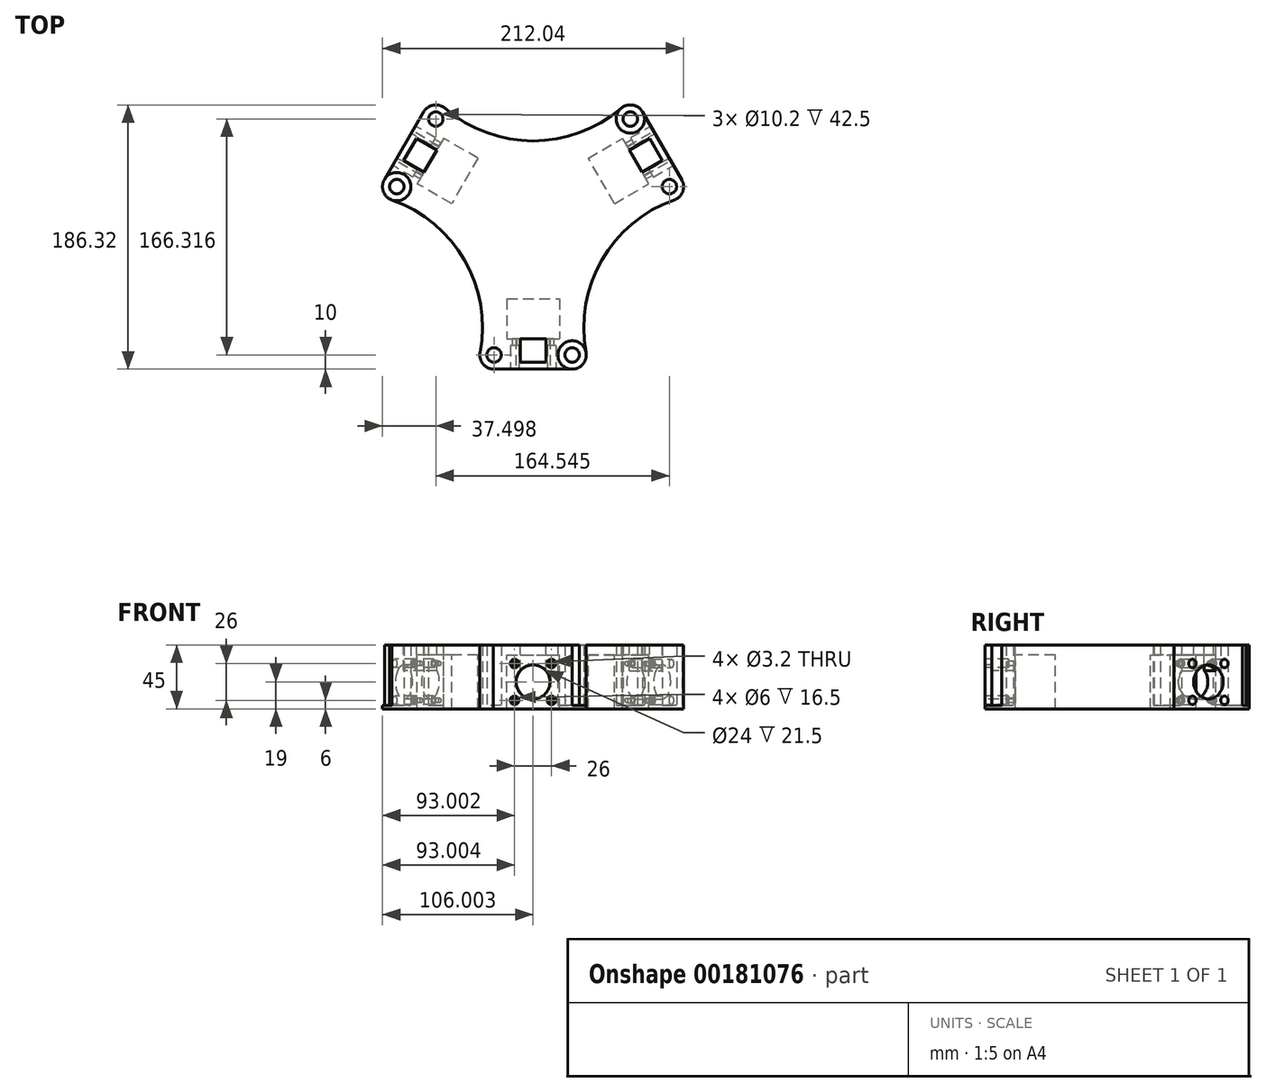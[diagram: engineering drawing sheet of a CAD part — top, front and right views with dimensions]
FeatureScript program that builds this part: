
annotation { "Feature Type Name" : "Feature", "Feature Type Description" : "" }
export const myFeature = defineFeature(function(context is Context, id is Id, definition is map)
    precondition{}
    {
        {
            var Q0;
            Q0=qCreatedBy(makeId("Top.planeOp"),FACE);
            var sketch = newSketch(context, id + "F0", { "sketchPlane" : qUnion([Q0])});
            skCircle(sketch, "E0", {"center": v(0, 0) * mm, "radius": 57.15 * mm, "construction": true});
            skLineSegment(sketch, "E1.bottom", {"start": v(110, -110) * mm, "end": v(-110, -110) * mm, "construction": true});
            skLineSegment(sketch, "E1.top", {"start": v(110, 110) * mm, "end": v(-110, 110) * mm, "construction": true});
            skLineSegment(sketch, "E1.left", {"start": v(110, -110) * mm, "end": v(110, 110) * mm, "construction": true});
            skLineSegment(sketch, "E1.right", {"start": v(-110, -110) * mm, "end": v(-110, 110) * mm, "construction": true});
            skLineSegment(sketch, "E2", {"start": v(0, 0) * mm, "end": v(-80.99, -46.76) * mm});
            skLineSegment(sketch, "E3", {"start": v(0, 0) * mm, "end": v(-84.59, 48.84) * mm});
            skLineSegment(sketch, "E4", {"start": v(0, 0) * mm, "end": v(0, -95) * mm});
            skLineSegment(sketch, "E5.MirrorCS", {"start": v(0, 0) * mm, "end": v(80.99, -46.76) * mm});
            skLineSegment(sketch, "E6.MirrorCS", {"start": v(0, 0) * mm, "end": v(84.59, 48.84) * mm});
            skCircle(sketch, "E7", {"center": v(-27.5, -95) * mm, "radius": 5.1 * mm});
            skCircle(sketch, "E8", {"center": v(-27.5, -95) * mm, "radius": 10 * mm});
            skCircle(sketch, "E9.MirrorC", {"center": v(27.5, -95) * mm, "radius": 10 * mm});
            skCircle(sketch, "E10.MirrorC", {"center": v(27.5, -95) * mm, "radius": 5.1 * mm});
            skLineSegment(sketch, "E11", {"start": v(-27.95, -104.99) * mm, "end": v(27.5, -105) * mm});
            skCircle(sketch, "E12.1.0", {"center": v(68.52, 71.32) * mm, "radius": 5.1 * mm});
            skCircle(sketch, "E12.1.1", {"center": v(68.52, 71.32) * mm, "radius": 10 * mm});
            skLineSegment(sketch, "E12.1.2", {"start": v(104.9, 28.3) * mm, "end": v(77.18, 76.31) * mm});
            skCircle(sketch, "E12.1.3", {"center": v(96.02, 23.68) * mm, "radius": 10 * mm});
            skCircle(sketch, "E12.1.4", {"center": v(96.02, 23.68) * mm, "radius": 5.1 * mm});
            skCircle(sketch, "E12.2.0", {"center": v(-96.02, 23.68) * mm, "radius": 5.1 * mm});
            skCircle(sketch, "E12.2.1", {"center": v(-96.02, 23.68) * mm, "radius": 10 * mm});
            skLineSegment(sketch, "E12.2.2", {"start": v(-76.95, 76.7) * mm, "end": v(-104.68, 28.69) * mm});
            skCircle(sketch, "E12.2.3", {"center": v(-68.52, 71.32) * mm, "radius": 10 * mm});
            skCircle(sketch, "E12.2.4", {"center": v(-68.52, 71.32) * mm, "radius": 5.1 * mm});
            skArc(sketch, "E13", {"start": v(99.32, 14.24) * mm, "mid": v(48.39, -27.94) * mm, "end": v(37.32, -93.14) * mm});
            skArc(sketch, "E14.1.0", {"start": v(-62, 78.9) * mm, "mid": v(0, 55.87) * mm, "end": v(62, 78.9) * mm});
            skArc(sketch, "E14.2.0", {"start": v(-37.32, -93.14) * mm, "mid": v(-48.39, -27.94) * mm, "end": v(-99.32, 14.24) * mm});
            skSolve(sketch);
        }
        {
            var Q0;
            {var subQ9=sQuery(id+"F0.wireOp",EDGE,"E5.MirrorCS");var subQ10=sQuery(id+"F0.wireOp",EDGE,"E2");var subQ11=makeQuery(id+"F0.imprint","INTERSECT",VERTEX,{"derivedFrom":[subQ10,subQ9]});Q0=makeQuery(id+"F0.imprint","IMPRINT",FACE,{"disambiguationData":[TD([[makeQuery(id+"F0.imprint","IMPRINT",EDGE,{"disambiguationData":[TD([[subQ11,-1.0]])],"derivedFrom":subQ10}),1.0]])]});}
            var Q1;
            Q1=makeQuery(id+"F0.imprint","IMPRINT",FACE,{"disambiguationData":[TD([[makeQuery(id+"F0.imprint","IMPRINT",EDGE,{"derivedFrom":sQuery(id+"F0.wireOp",EDGE,"E10.MirrorC")}),1.0]])]});
            var Q2;
            Q2=makeQuery(id+"F0.imprint","IMPRINT",FACE,{"disambiguationData":[TD([[makeQuery(id+"F0.imprint","IMPRINT",EDGE,{"derivedFrom":sQuery(id+"F0.wireOp",EDGE,"E7")}),-1.0]])]});
            extrude(context, id + "F1", {"entities" : qUnion([Q0, Q1, Q2]), "depth" : 45 * mm});
        }
        {
            var Q0;
            Q0=makeQuery(id+"F0.imprint","IMPRINT",FACE,{"disambiguationData":[TD([[makeQuery(id+"F0.imprint","IMPRINT",EDGE,{"derivedFrom":sQuery(id+"F0.wireOp",EDGE,"E10.MirrorC")}),-1.0]])]});
            var Q1;
            Q1=makeQuery(id+"F0.imprint","IMPRINT",FACE,{"disambiguationData":[TD([[makeQuery(id+"F0.imprint","IMPRINT",EDGE,{"derivedFrom":sQuery(id+"F0.wireOp",EDGE,"E7")}),1.0]])]});
            extrude(context, id + "F2", {"entities" : qUnion([Q0, Q1]), "operationType" : NewBodyOperationType.ADD, "depth" : 2.5 * mm});
        }
        {
            var Q0;
            Q0=makeQuery(id+"F1.opExtrude","SWEPT_FACE",FACE,{"disambiguationData":[OSD([sQuery(id+"F0.wireOp",EDGE,"E11")])]});
            cPlane(context, id + "F3", {"entities" : qUnion([Q0]), "cplaneType" : CPlaneType.OFFSET, "offset" : 16.5 * mm, "oppositeDirection" : true, "width" : 150 * mm, "height" : 150 * mm});
        }
        {
            var Q0;
            Q0=qCreatedBy(id+"F3.planeOp",FACE);
            var sketch = newSketch(context, id + "F4", { "sketchPlane" : qUnion([Q0])});
            skLineSegment(sketch, "E15.0.1", {"start": v(27.52, 0) * mm, "end": v(27.52, 45) * mm});
            skLineSegment(sketch, "E15.0.2", {"start": v(27.52, 45) * mm, "end": v(-27.93, 45) * mm});
            skLineSegment(sketch, "E15.0.3", {"start": v(-27.93, 45) * mm, "end": v(-27.93, 0) * mm});
            skCircle(sketch, "E16", {"center": v(0, 19) * mm, "radius": 12 * mm});
            skLineSegment(sketch, "E17.bottom", {"start": v(13, 6) * mm, "end": v(-13, 6) * mm, "construction": true});
            skLineSegment(sketch, "E17.top", {"start": v(13, 32) * mm, "end": v(-13, 32) * mm, "construction": true});
            skLineSegment(sketch, "E17.left", {"start": v(13, 6) * mm, "end": v(13, 32) * mm, "construction": true});
            skLineSegment(sketch, "E17.right", {"start": v(-13, 6) * mm, "end": v(-13, 32) * mm, "construction": true});
            skCircle(sketch, "E18", {"center": v(-13, 32) * mm, "radius": 1.6 * mm});
            skCircle(sketch, "E19", {"center": v(13, 32) * mm, "radius": 1.6 * mm});
            skCircle(sketch, "E20", {"center": v(13, 6) * mm, "radius": 1.6 * mm});
            skCircle(sketch, "E21", {"center": v(-13, 6) * mm, "radius": 1.6 * mm});
            skLineSegment(sketch, "E22", {"start": v(-27.93, 0) * mm, "end": v(27.52, 0) * mm, "construction": true});
            skLineSegment(sketch, "E23.bottom", {"start": v(-18.5, 0) * mm, "end": v(18.5, 0) * mm});
            skLineSegment(sketch, "E23.top", {"start": v(-18.5, 38) * mm, "end": v(18.5, 38) * mm});
            skLineSegment(sketch, "E23.left", {"start": v(-18.5, 0) * mm, "end": v(-18.5, 38) * mm});
            skLineSegment(sketch, "E23.right", {"start": v(18.5, 0) * mm, "end": v(18.5, 38) * mm});
            skPoint(sketch, "E24", {"position": v(-18.5, 19) * mm});
            skSolve(sketch);
        }
        {
            var Q0;
            Q0=makeQuery(id+"F1.opExtrude","SWEPT_FACE",FACE,{"disambiguationData":[OSD([sQuery(id+"F0.wireOp",EDGE,"E11")])]});
            var sketch = newSketch(context, id + "F5", { "sketchPlane" : qUnion([Q0])});
            skCircle(sketch, "E25.0", {"center": v(-13, 32) * mm, "radius": 1.6 * mm, "construction": true});
            skCircle(sketch, "E26.0", {"center": v(13, 32) * mm, "radius": 1.6 * mm, "construction": true});
            skCircle(sketch, "E27.0", {"center": v(13, 6) * mm, "radius": 1.6 * mm, "construction": true});
            skCircle(sketch, "E28.0", {"center": v(-13, 6) * mm, "radius": 1.6 * mm, "construction": true});
            skCircle(sketch, "E29", {"center": v(-13, 32) * mm, "radius": 3 * mm});
            skCircle(sketch, "E30", {"center": v(13, 32) * mm, "radius": 3 * mm});
            skCircle(sketch, "E31", {"center": v(13, 6) * mm, "radius": 3 * mm});
            skCircle(sketch, "E32", {"center": v(-13, 6) * mm, "radius": 3 * mm});
            skSolve(sketch);
        }
        {
            var Q0;
            Q0=makeQuery(id+"F4.imprint","IMPRINT",FACE,{"disambiguationData":[TD([[makeQuery(id+"F4.imprint","IMPRINT",EDGE,{"derivedFrom":sQuery(id+"F4.wireOp",EDGE,"E16")}),-1.0]])]});
            var Q1;
            Q1=makeQuery(id+"F4.imprint","IMPRINT",FACE,{"disambiguationData":[TD([[makeQuery(id+"F4.imprint","IMPRINT",EDGE,{"derivedFrom":sQuery(id+"F4.wireOp",EDGE,"E16")}),1.0]])]});
            var Q2;
            Q2=makeQuery(id+"F4.imprint","IMPRINT",FACE,{"disambiguationData":[TD([[makeQuery(id+"F4.imprint","IMPRINT",EDGE,{"derivedFrom":sQuery(id+"F4.wireOp",EDGE,"E18")}),1.0]])]});
            var Q3;
            Q3=makeQuery(id+"F4.imprint","IMPRINT",FACE,{"disambiguationData":[TD([[makeQuery(id+"F4.imprint","IMPRINT",EDGE,{"derivedFrom":sQuery(id+"F4.wireOp",EDGE,"E19")}),1.0]])]});
            var Q4;
            Q4=makeQuery(id+"F4.imprint","IMPRINT",FACE,{"disambiguationData":[TD([[makeQuery(id+"F4.imprint","IMPRINT",EDGE,{"derivedFrom":sQuery(id+"F4.wireOp",EDGE,"E20")}),1.0]])]});
            var Q5;
            Q5=makeQuery(id+"F4.imprint","IMPRINT",FACE,{"disambiguationData":[TD([[makeQuery(id+"F4.imprint","IMPRINT",EDGE,{"derivedFrom":sQuery(id+"F4.wireOp",EDGE,"E21")}),1.0]])]});
            extrude(context, id + "F6", {"entities" : qUnion([Q0, Q1, Q2, Q3, Q4, Q5]), "operationType" : NewBodyOperationType.REMOVE, "oppositeDirection" : true, "depth" : 33 * mm, "hasSecondDirection" : true, "secondDirectionOppositeDirection" : true, "secondDirectionDepth" : 5 * mm});
        }
        {
            var Q0;
            Q0=makeQuery(id+"F4.imprint","IMPRINT",FACE,{"disambiguationData":[TD([[makeQuery(id+"F4.imprint","IMPRINT",EDGE,{"derivedFrom":sQuery(id+"F4.wireOp",EDGE,"E16")}),1.0]])]});
            var Q1;
            Q1=makeQuery(id+"F4.imprint","IMPRINT",FACE,{"disambiguationData":[TD([[makeQuery(id+"F4.imprint","IMPRINT",EDGE,{"derivedFrom":sQuery(id+"F4.wireOp",EDGE,"E18")}),1.0]])]});
            var Q2;
            Q2=makeQuery(id+"F4.imprint","IMPRINT",FACE,{"disambiguationData":[TD([[makeQuery(id+"F4.imprint","IMPRINT",EDGE,{"derivedFrom":sQuery(id+"F4.wireOp",EDGE,"E19")}),1.0]])]});
            var Q3;
            Q3=makeQuery(id+"F4.imprint","IMPRINT",FACE,{"disambiguationData":[TD([[makeQuery(id+"F4.imprint","IMPRINT",EDGE,{"derivedFrom":sQuery(id+"F4.wireOp",EDGE,"E21")}),1.0]])]});
            var Q4;
            Q4=makeQuery(id+"F4.imprint","IMPRINT",FACE,{"disambiguationData":[TD([[makeQuery(id+"F4.imprint","IMPRINT",EDGE,{"derivedFrom":sQuery(id+"F4.wireOp",EDGE,"E20")}),1.0]])]});
            var Q5;
            Q5=makeQuery(id+"F6.boolean.opBoolean","COPY",FACE,{"derivedFrom":makeQuery(id+"F6.opExtrude","CAP_FACE",FACE,{"disambiguationData":[OSD([sQuery(id+"F4.wireOp",EDGE,"E23.bottom"),sQuery(id+"F4.wireOp",EDGE,"E23.top"),sQuery(id+"F4.wireOp",EDGE,"E23.left"),sQuery(id+"F4.wireOp",EDGE,"E23.right")])],"isStart":true})});
            var Q6;
            Q6=makeQuery(id+"F1.opExtrude","SWEPT_FACE",FACE,{"disambiguationData":[OSD([sQuery(id+"F0.wireOp",EDGE,"E11")])]});
            extrude(context, id + "F7", {"entities" : qUnion([Q0, Q1, Q2, Q3, Q4]), "operationType" : NewBodyOperationType.REMOVE, "endBound" : BoundingType.UP_TO_SURFACE, "oppositeDirection" : true, "endBoundEntityFace" : qUnion([Q5]), "depth" : 25 * mm, "hasSecondDirection" : true, "secondDirectionBound" : SecondDirectionBoundingType.UP_TO_SURFACE, "secondDirectionOppositeDirection" : false, "secondDirectionBoundEntityFace" : qUnion([Q6]), "secondDirectionDepth" : 25 * mm});
        }
        {
            var Q0;
            Q0=makeQuery(id+"F5.imprint","IMPRINT",FACE,{"disambiguationData":[TD([[makeQuery(id+"F5.imprint","IMPRINT",EDGE,{"derivedFrom":sQuery(id+"F5.wireOp",EDGE,"E29")}),1.0]])]});
            var Q1;
            Q1=makeQuery(id+"F5.imprint","IMPRINT",FACE,{"disambiguationData":[TD([[makeQuery(id+"F5.imprint","IMPRINT",EDGE,{"derivedFrom":sQuery(id+"F5.wireOp",EDGE,"E30")}),1.0]])]});
            var Q2;
            Q2=makeQuery(id+"F5.imprint","IMPRINT",FACE,{"disambiguationData":[TD([[makeQuery(id+"F5.imprint","IMPRINT",EDGE,{"derivedFrom":sQuery(id+"F5.wireOp",EDGE,"E31")}),1.0]])]});
            var Q3;
            Q3=makeQuery(id+"F5.imprint","IMPRINT",FACE,{"disambiguationData":[TD([[makeQuery(id+"F5.imprint","IMPRINT",EDGE,{"derivedFrom":sQuery(id+"F5.wireOp",EDGE,"E32")}),1.0]])]});
            extrude(context, id + "F8", {"entities" : qUnion([Q0, Q1, Q2, Q3]), "operationType" : NewBodyOperationType.REMOVE, "oppositeDirection" : true, "depth" : 16.5 * mm});
        }
        {
            var Q0;
            Q0=makeQuery(id+"F1.opExtrude","CAP_FACE",FACE,{"disambiguationData":[OSD([sQuery(id+"F0.wireOp",EDGE,"E2"),sQuery(id+"F0.wireOp",EDGE,"E5.MirrorCS"),sQuery(id+"F0.wireOp",EDGE,"E7"),sQuery(id+"F0.wireOp",EDGE,"E8"),sQuery(id+"F0.wireOp",EDGE,"E9.MirrorC"),sQuery(id+"F0.wireOp",EDGE,"E10.MirrorC"),sQuery(id+"F0.wireOp",EDGE,"E11"),sQuery(id+"F0.wireOp",EDGE,"E13"),sQuery(id+"F0.wireOp",EDGE,"E14.2.0")])],"isStart":false});
            var sketch = newSketch(context, id + "F9", { "sketchPlane" : qUnion([Q0])});
            skCircle(sketch, "E33.0", {"center": v(-27.5, -95) * mm, "radius": 5.1 * mm});
            skCircle(sketch, "E34.0", {"center": v(27.5, -95) * mm, "radius": 5.1 * mm});
            skLineSegment(sketch, "E35.0", {"start": v(-18.52, -83.5) * mm, "end": v(18.48, -83.5) * mm});
            skLineSegment(sketch, "E36", {"start": v(-27.5, -95) * mm, "end": v(27.5, -95) * mm, "construction": true});
            skLineSegment(sketch, "E37.bottom", {"start": v(9, -100) * mm, "end": v(-9, -100) * mm});
            skLineSegment(sketch, "E37.top", {"start": v(9, -90) * mm, "end": v(-9, -90) * mm});
            skLineSegment(sketch, "E37.left", {"start": v(9, -100) * mm, "end": v(9, -83.5) * mm});
            skLineSegment(sketch, "E37.right", {"start": v(-9, -100) * mm, "end": v(-9, -83.5) * mm});
            skPoint(sketch, "E37.middle", {"position": v(0, -95) * mm});
            skSolve(sketch);
        }
        {
            var Q0;
            {var subQ5=sQuery(id+"F9.wireOp",EDGE,"E37.top");Q0=makeQuery(id+"F9.imprint","IMPRINT",FACE,{"disambiguationData":[TD([[makeQuery(id+"F9.imprint","IMPRINT",EDGE,{"derivedFrom":subQ5}),-1.0]])]});}
            var Q1;
            {var subQ0=sQuery(id+"F9.wireOp",EDGE,"E37.bottom");Q1=makeQuery(id+"F9.imprint","IMPRINT",FACE,{"disambiguationData":[TD([[makeQuery(id+"F9.imprint","IMPRINT",EDGE,{"derivedFrom":subQ0}),-1.0]])]});}
            var Q2;
            Q2=makeQuery(id+"F7.boolean.opBoolean","COPY",FACE,{"derivedFrom":makeQuery(id+"F7.opExtrude","SWEPT_FACE",FACE,{"disambiguationData":[OSD([sQuery(id+"F4.wireOp",EDGE,"E16")])]})});
            extrude(context, id + "F10", {"entities" : qUnion([Q0, Q1]), "operationType" : NewBodyOperationType.REMOVE, "endBound" : BoundingType.UP_TO_SURFACE, "oppositeDirection" : true, "endBoundEntityFace" : qUnion([Q2]), "depth" : 25 * mm});
        }
        {
            var Q0;
            Q0=makeQuery(id+"F1.opExtrude","SWEPT_BODY",BODY,{"disambiguationData":[OSD([sQuery(id+"F0.wireOp",EDGE,"E2"),sQuery(id+"F0.wireOp",EDGE,"E5.MirrorCS"),sQuery(id+"F0.wireOp",EDGE,"E7"),sQuery(id+"F0.wireOp",EDGE,"E8"),sQuery(id+"F0.wireOp",EDGE,"E9.MirrorC"),sQuery(id+"F0.wireOp",EDGE,"E10.MirrorC"),sQuery(id+"F0.wireOp",EDGE,"E11"),sQuery(id+"F0.wireOp",EDGE,"E13"),sQuery(id+"F0.wireOp",EDGE,"E14.2.0")])]});
            var Q1;
            Q1=sQuery(id+"F0.wireOp",EDGE,"E0");
            circularPattern(context, id + "F11", {"operationType" : NewBodyOperationType.ADD, "entities" : qUnion([Q0]), "axis" : qUnion([Q1]), "angle" : 240 * degree, "instanceCount" : 3});
        }
    });
